# Revit family: Domotics-DomesticRanges-GEWISS-CHORUS_POWER-SOCKET-OUTLET_SHAVER
name_source: partatom
category: Apparecchi elettrici
revit_build: Autodesk Revit 2016 (Build: 20161004_0715(x64)
units: mm (PartAtom-declared; Revit-internal decimal feet)

## family parameters
Condiviso = Sì
Host = Superficie
Mantenere orientamento annotazione = Sì
Numero OmniClass = 23.80.50.11.14
Punto di calcolo locali = Sì
Quota connettore circolare = Usa diametro
Taglio con vuoti quando caricato = Sì
Tipo di parte = Normale
Titolo OmniClass = Switches

## types (3) — shared parameters
Catalogue = DOMOTICS
Catalogue Range = CHORUS - DOMESTIC RANGE
Category = Shaver socket-outlet
Description. = Shaver socket-outlet
Description: = With isolation transformer
Electrocod = 0131
Finitura pulsante = titanio
For plug pins = Ã˜ 4 / 5 - 6.3x1.5 mm
IDF = 7bb0a994-ccc8-431f-8470-e9729077d296
IDT = d9f9e070-7523-4648-90a7-3128a0033d74
Insulation resistance = > 5 MOhm
L = 69 mm  [stored 0.226378 ft]
Maximum power = 20VA
No. Chorus modules = 3
No. Chorus modules: = 3
Produttore = GEWISS S.p.A.
Prospetto di default = 1219 mm
Resistance at test voltage = 2000 V at 50 Hz for 1 minute
SEO = Socket outlet
Selectable output voltage = 120-230V ac
Socket-out type = P11-USA
Standard = Euro-USA
Standard: = Euro-American
Standard; = IEC 60884-1; EN 61558-2-5
Supply voltage = 230 V ac - 50/60 Hz
Technical sheet = https://www.gewiss.com
Terminal grip on cable traction = > 50 N
Terminal tightening capacity flexible cables (mm2) = min. 0,75 - max. 2x4
Terminal tightening capacity rigid cables (mm2) = min. 0,5 - max. 2x2,5
Thermo-pressure with ball = 125
Type = For razor
URL = https://www.gewiss.com
Version file RFA = 19.0
Voltage = 230V ac
Wiring terminals = With screw
finitura = titanio
sp = 26 mm  [stored 0.0853018 ft]
w = 46 mm  [stored 0.150919 ft]
zero-valued in all types: Distanza_x, tipologia

## per-type parameters (varying)
| type | Colour | Descrizione | EAN code | Modello |
| GW12331 - Shaver socket eu/usa 3M Black | Black | SHAVER SOCKET+INSULATION TRANSF 3M B | 8011564267367 | GW12331 |
| GW10331 - Shaver socket eu/usa 3M White | White | SHAVER SOCKET EU/USA W. INS TRANSF 3M W | 8011564262515 | GW10331 |
| GW14331 - Shaver socket eu/usa 3M Titanium | Titanium | SHAVER SOCKET+INSULATION TRANSF 3M T | 8011564266735 | GW14331 |

note: source unit labels omitted for Thermo-pressure with ball — the stored unit's dimension contradicts the parameter name (converter mislabeling)

note: [stored X ft] marks values corroborated as IEEE doubles in the binary element streams (Revit-internal decimal feet)

## geometry (parser evidence)
native form markers: Sweep x1
no freeform markers — native parametric forms only
